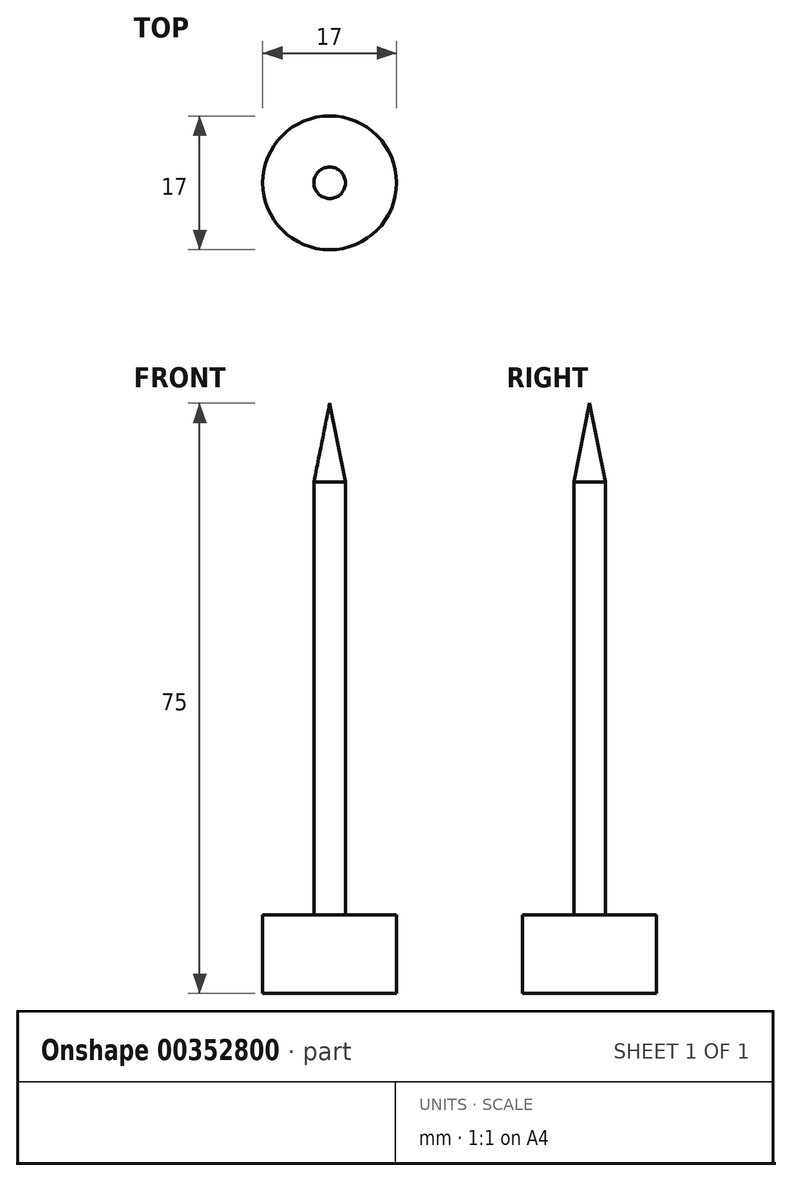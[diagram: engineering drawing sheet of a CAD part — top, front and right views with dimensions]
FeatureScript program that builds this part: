
annotation { "Feature Type Name" : "Feature", "Feature Type Description" : "" }
export const myFeature = defineFeature(function(context is Context, id is Id, definition is map)
    precondition{}
    {
        {
            var Q0;
            Q0=qCreatedBy(makeId("Front.planeOp"),FACE);
            var sketch = newSketch(context, id + "F0", { "sketchPlane" : qUnion([Q0])});
            skLineSegment(sketch, "E0", {"start": v(0, 0) * mm, "end": v(0, 75) * mm});
            skLineSegment(sketch, "E1", {"start": v(0, 0) * mm, "end": v(8.5, 0) * mm});
            skLineSegment(sketch, "E2", {"start": v(8.5, 0) * mm, "end": v(8.5, 10) * mm});
            skLineSegment(sketch, "E3", {"start": v(8.5, 10) * mm, "end": v(2, 10) * mm});
            skLineSegment(sketch, "E4", {"start": v(2, 10) * mm, "end": v(2, 65) * mm});
            skLineSegment(sketch, "E5", {"start": v(2, 65) * mm, "end": v(0, 75) * mm});
            skSolve(sketch);
        }
        {
            var Q0;
            Q0=makeQuery(id+"F0.imprint","IMPRINT",FACE,{"disambiguationData":[TD([[makeQuery(id+"F0.imprint","IMPRINT",EDGE,{"derivedFrom":sQuery(id+"F0.wireOp",EDGE,"E0")}),-1.0]])]});
            var Q1;
            Q1=sQuery(id+"F0.wireOp",EDGE,"E0");
            revolve(context, id + "F1", {"entities" : qUnion([Q0]), "axis" : qUnion([Q1]), "revolveType" : RevolveType.FULL});
        }
    });
